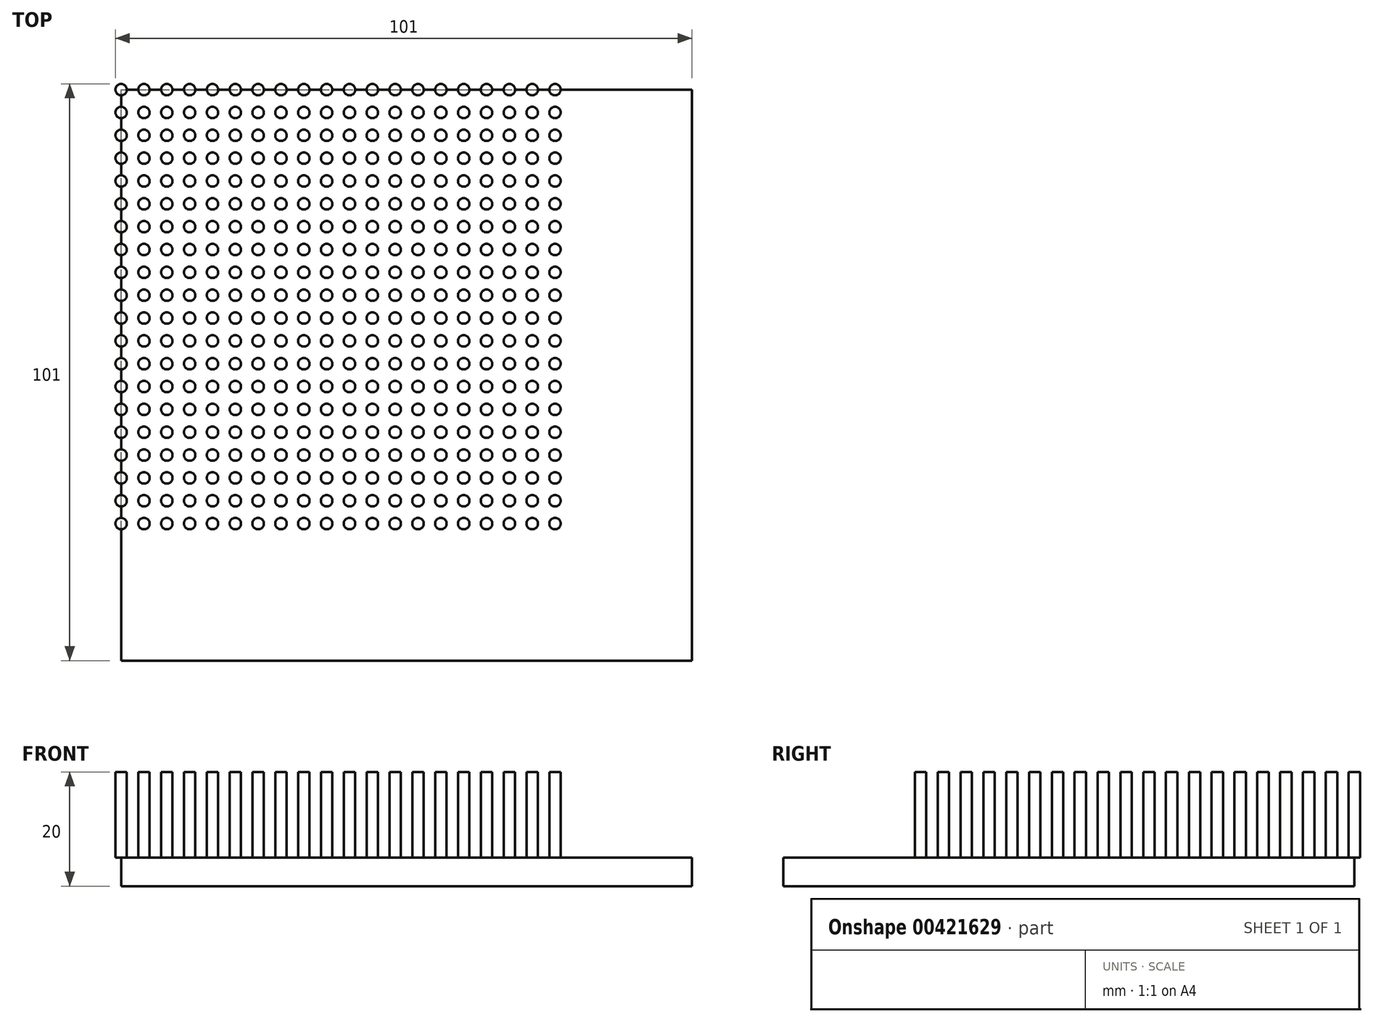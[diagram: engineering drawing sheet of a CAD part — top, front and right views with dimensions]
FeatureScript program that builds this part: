
annotation { "Feature Type Name" : "Feature", "Feature Type Description" : "" }
export const myFeature = defineFeature(function(context is Context, id is Id, definition is map)
    precondition{}
    {
        {
            var Q0;
            Q0=qCreatedBy(makeId("Top.planeOp"),FACE);
            var sketch = newSketch(context, id + "F0", { "sketchPlane" : qUnion([Q0])});
            skLineSegment(sketch, "E0.bottom", {"start": v(0, 0) * mm, "end": v(100, 0) * mm});
            skLineSegment(sketch, "E0.top", {"start": v(0, 100) * mm, "end": v(100, 100) * mm});
            skLineSegment(sketch, "E0.left", {"start": v(0, 0) * mm, "end": v(0, 100) * mm});
            skLineSegment(sketch, "E0.right", {"start": v(100, 0) * mm, "end": v(100, 100) * mm});
            skSolve(sketch);
        }
        {
            var Q0;
            Q0 = qSketchRegion(id + "F0", true);
            extrude(context, id + "F1", {"entities" : qUnion([Q0]), "depth" : 5 * mm});
        }
        {
            var Q0;
            Q0=makeQuery(id+"F1.opExtrude","CAP_FACE",FACE,{"disambiguationData":[OSD([sQuery(id+"F0.wireOp",EDGE,"E0.bottom"),sQuery(id+"F0.wireOp",EDGE,"E0.top"),sQuery(id+"F0.wireOp",EDGE,"E0.left"),sQuery(id+"F0.wireOp",EDGE,"E0.right")])],"isStart":false});
            var sketch = newSketch(context, id + "F2", { "sketchPlane" : qUnion([Q0])});
            skCircle(sketch, "E1", {"center": v(0, 100) * mm, "radius": 1 * mm});
            skCircle(sketch, "E2.0.1.0", {"center": v(0, 96) * mm, "radius": 1 * mm});
            skCircle(sketch, "E2.0.2.0", {"center": v(0, 92) * mm, "radius": 1 * mm});
            skCircle(sketch, "E2.0.3.0", {"center": v(0, 88) * mm, "radius": 1 * mm});
            skCircle(sketch, "E2.0.4.0", {"center": v(0, 84) * mm, "radius": 1 * mm});
            skCircle(sketch, "E2.0.5.0", {"center": v(0, 80) * mm, "radius": 1 * mm});
            skCircle(sketch, "E2.0.6.0", {"center": v(0, 76) * mm, "radius": 1 * mm});
            skCircle(sketch, "E2.0.7.0", {"center": v(0, 72) * mm, "radius": 1 * mm});
            skCircle(sketch, "E2.0.8.0", {"center": v(0, 68) * mm, "radius": 1 * mm});
            skCircle(sketch, "E2.0.9.0", {"center": v(0, 64) * mm, "radius": 1 * mm});
            skCircle(sketch, "E2.0.10.0", {"center": v(0, 60) * mm, "radius": 1 * mm});
            skCircle(sketch, "E2.0.11.0", {"center": v(0, 56) * mm, "radius": 1 * mm});
            skCircle(sketch, "E2.0.12.0", {"center": v(0, 52) * mm, "radius": 1 * mm});
            skCircle(sketch, "E2.0.13.0", {"center": v(0, 48) * mm, "radius": 1 * mm});
            skCircle(sketch, "E2.0.14.0", {"center": v(0, 44) * mm, "radius": 1 * mm});
            skCircle(sketch, "E2.0.15.0", {"center": v(0, 40) * mm, "radius": 1 * mm});
            skCircle(sketch, "E2.0.16.0", {"center": v(0, 36) * mm, "radius": 1 * mm});
            skCircle(sketch, "E2.0.17.0", {"center": v(0, 32) * mm, "radius": 1 * mm});
            skCircle(sketch, "E2.0.18.0", {"center": v(0, 28) * mm, "radius": 1 * mm});
            skCircle(sketch, "E2.0.19.0", {"center": v(0, 24) * mm, "radius": 1 * mm});
            skCircle(sketch, "E2.1.0.0", {"center": v(4, 100) * mm, "radius": 1 * mm});
            skCircle(sketch, "E2.1.1.0", {"center": v(4, 96) * mm, "radius": 1 * mm});
            skCircle(sketch, "E2.1.2.0", {"center": v(4, 92) * mm, "radius": 1 * mm});
            skCircle(sketch, "E2.1.3.0", {"center": v(4, 88) * mm, "radius": 1 * mm});
            skCircle(sketch, "E2.1.4.0", {"center": v(4, 84) * mm, "radius": 1 * mm});
            skCircle(sketch, "E2.1.5.0", {"center": v(4, 80) * mm, "radius": 1 * mm});
            skCircle(sketch, "E2.1.6.0", {"center": v(4, 76) * mm, "radius": 1 * mm});
            skCircle(sketch, "E2.1.7.0", {"center": v(4, 72) * mm, "radius": 1 * mm});
            skCircle(sketch, "E2.1.8.0", {"center": v(4, 68) * mm, "radius": 1 * mm});
            skCircle(sketch, "E2.1.9.0", {"center": v(4, 64) * mm, "radius": 1 * mm});
            skCircle(sketch, "E2.1.10.0", {"center": v(4, 60) * mm, "radius": 1 * mm});
            skCircle(sketch, "E2.1.11.0", {"center": v(4, 56) * mm, "radius": 1 * mm});
            skCircle(sketch, "E2.1.12.0", {"center": v(4, 52) * mm, "radius": 1 * mm});
            skCircle(sketch, "E2.1.13.0", {"center": v(4, 48) * mm, "radius": 1 * mm});
            skCircle(sketch, "E2.1.14.0", {"center": v(4, 44) * mm, "radius": 1 * mm});
            skCircle(sketch, "E2.1.15.0", {"center": v(4, 40) * mm, "radius": 1 * mm});
            skCircle(sketch, "E2.1.16.0", {"center": v(4, 36) * mm, "radius": 1 * mm});
            skCircle(sketch, "E2.1.17.0", {"center": v(4, 32) * mm, "radius": 1 * mm});
            skCircle(sketch, "E2.1.18.0", {"center": v(4, 28) * mm, "radius": 1 * mm});
            skCircle(sketch, "E2.1.19.0", {"center": v(4, 24) * mm, "radius": 1 * mm});
            skCircle(sketch, "E2.2.0.0", {"center": v(8, 100) * mm, "radius": 1 * mm});
            skCircle(sketch, "E2.2.1.0", {"center": v(8, 96) * mm, "radius": 1 * mm});
            skCircle(sketch, "E2.2.2.0", {"center": v(8, 92) * mm, "radius": 1 * mm});
            skCircle(sketch, "E2.2.3.0", {"center": v(8, 88) * mm, "radius": 1 * mm});
            skCircle(sketch, "E2.2.4.0", {"center": v(8, 84) * mm, "radius": 1 * mm});
            skCircle(sketch, "E2.2.5.0", {"center": v(8, 80) * mm, "radius": 1 * mm});
            skCircle(sketch, "E2.2.6.0", {"center": v(8, 76) * mm, "radius": 1 * mm});
            skCircle(sketch, "E2.2.7.0", {"center": v(8, 72) * mm, "radius": 1 * mm});
            skCircle(sketch, "E2.2.8.0", {"center": v(8, 68) * mm, "radius": 1 * mm});
            skCircle(sketch, "E2.2.9.0", {"center": v(8, 64) * mm, "radius": 1 * mm});
            skCircle(sketch, "E2.2.10.0", {"center": v(8, 60) * mm, "radius": 1 * mm});
            skCircle(sketch, "E2.2.11.0", {"center": v(8, 56) * mm, "radius": 1 * mm});
            skCircle(sketch, "E2.2.12.0", {"center": v(8, 52) * mm, "radius": 1 * mm});
            skCircle(sketch, "E2.2.13.0", {"center": v(8, 48) * mm, "radius": 1 * mm});
            skCircle(sketch, "E2.2.14.0", {"center": v(8, 44) * mm, "radius": 1 * mm});
            skCircle(sketch, "E2.2.15.0", {"center": v(8, 40) * mm, "radius": 1 * mm});
            skCircle(sketch, "E2.2.16.0", {"center": v(8, 36) * mm, "radius": 1 * mm});
            skCircle(sketch, "E2.2.17.0", {"center": v(8, 32) * mm, "radius": 1 * mm});
            skCircle(sketch, "E2.2.18.0", {"center": v(8, 28) * mm, "radius": 1 * mm});
            skCircle(sketch, "E2.2.19.0", {"center": v(8, 24) * mm, "radius": 1 * mm});
            skCircle(sketch, "E2.3.0.0", {"center": v(12, 100) * mm, "radius": 1 * mm});
            skCircle(sketch, "E2.3.1.0", {"center": v(12, 96) * mm, "radius": 1 * mm});
            skCircle(sketch, "E2.3.2.0", {"center": v(12, 92) * mm, "radius": 1 * mm});
            skCircle(sketch, "E2.3.3.0", {"center": v(12, 88) * mm, "radius": 1 * mm});
            skCircle(sketch, "E2.3.4.0", {"center": v(12, 84) * mm, "radius": 1 * mm});
            skCircle(sketch, "E2.3.5.0", {"center": v(12, 80) * mm, "radius": 1 * mm});
            skCircle(sketch, "E2.3.6.0", {"center": v(12, 76) * mm, "radius": 1 * mm});
            skCircle(sketch, "E2.3.7.0", {"center": v(12, 72) * mm, "radius": 1 * mm});
            skCircle(sketch, "E2.3.8.0", {"center": v(12, 68) * mm, "radius": 1 * mm});
            skCircle(sketch, "E2.3.9.0", {"center": v(12, 64) * mm, "radius": 1 * mm});
            skCircle(sketch, "E2.3.10.0", {"center": v(12, 60) * mm, "radius": 1 * mm});
            skCircle(sketch, "E2.3.11.0", {"center": v(12, 56) * mm, "radius": 1 * mm});
            skCircle(sketch, "E2.3.12.0", {"center": v(12, 52) * mm, "radius": 1 * mm});
            skCircle(sketch, "E2.3.13.0", {"center": v(12, 48) * mm, "radius": 1 * mm});
            skCircle(sketch, "E2.3.14.0", {"center": v(12, 44) * mm, "radius": 1 * mm});
            skCircle(sketch, "E2.3.15.0", {"center": v(12, 40) * mm, "radius": 1 * mm});
            skCircle(sketch, "E2.3.16.0", {"center": v(12, 36) * mm, "radius": 1 * mm});
            skCircle(sketch, "E2.3.17.0", {"center": v(12, 32) * mm, "radius": 1 * mm});
            skCircle(sketch, "E2.3.18.0", {"center": v(12, 28) * mm, "radius": 1 * mm});
            skCircle(sketch, "E2.3.19.0", {"center": v(12, 24) * mm, "radius": 1 * mm});
            skCircle(sketch, "E2.4.0.0", {"center": v(16, 100) * mm, "radius": 1 * mm});
            skCircle(sketch, "E2.4.1.0", {"center": v(16, 96) * mm, "radius": 1 * mm});
            skCircle(sketch, "E2.4.2.0", {"center": v(16, 92) * mm, "radius": 1 * mm});
            skCircle(sketch, "E2.4.3.0", {"center": v(16, 88) * mm, "radius": 1 * mm});
            skCircle(sketch, "E2.4.4.0", {"center": v(16, 84) * mm, "radius": 1 * mm});
            skCircle(sketch, "E2.4.5.0", {"center": v(16, 80) * mm, "radius": 1 * mm});
            skCircle(sketch, "E2.4.6.0", {"center": v(16, 76) * mm, "radius": 1 * mm});
            skCircle(sketch, "E2.4.7.0", {"center": v(16, 72) * mm, "radius": 1 * mm});
            skCircle(sketch, "E2.4.8.0", {"center": v(16, 68) * mm, "radius": 1 * mm});
            skCircle(sketch, "E2.4.9.0", {"center": v(16, 64) * mm, "radius": 1 * mm});
            skCircle(sketch, "E2.4.10.0", {"center": v(16, 60) * mm, "radius": 1 * mm});
            skCircle(sketch, "E2.4.11.0", {"center": v(16, 56) * mm, "radius": 1 * mm});
            skCircle(sketch, "E2.4.12.0", {"center": v(16, 52) * mm, "radius": 1 * mm});
            skCircle(sketch, "E2.4.13.0", {"center": v(16, 48) * mm, "radius": 1 * mm});
            skCircle(sketch, "E2.4.14.0", {"center": v(16, 44) * mm, "radius": 1 * mm});
            skCircle(sketch, "E2.4.15.0", {"center": v(16, 40) * mm, "radius": 1 * mm});
            skCircle(sketch, "E2.4.16.0", {"center": v(16, 36) * mm, "radius": 1 * mm});
            skCircle(sketch, "E2.4.17.0", {"center": v(16, 32) * mm, "radius": 1 * mm});
            skCircle(sketch, "E2.4.18.0", {"center": v(16, 28) * mm, "radius": 1 * mm});
            skCircle(sketch, "E2.4.19.0", {"center": v(16, 24) * mm, "radius": 1 * mm});
            skCircle(sketch, "E2.5.0.0", {"center": v(20, 100) * mm, "radius": 1 * mm});
            skCircle(sketch, "E2.5.1.0", {"center": v(20, 96) * mm, "radius": 1 * mm});
            skCircle(sketch, "E2.5.2.0", {"center": v(20, 92) * mm, "radius": 1 * mm});
            skCircle(sketch, "E2.5.3.0", {"center": v(20, 88) * mm, "radius": 1 * mm});
            skCircle(sketch, "E2.5.4.0", {"center": v(20, 84) * mm, "radius": 1 * mm});
            skCircle(sketch, "E2.5.5.0", {"center": v(20, 80) * mm, "radius": 1 * mm});
            skCircle(sketch, "E2.5.6.0", {"center": v(20, 76) * mm, "radius": 1 * mm});
            skCircle(sketch, "E2.5.7.0", {"center": v(20, 72) * mm, "radius": 1 * mm});
            skCircle(sketch, "E2.5.8.0", {"center": v(20, 68) * mm, "radius": 1 * mm});
            skCircle(sketch, "E2.5.9.0", {"center": v(20, 64) * mm, "radius": 1 * mm});
            skCircle(sketch, "E2.5.10.0", {"center": v(20, 60) * mm, "radius": 1 * mm});
            skCircle(sketch, "E2.5.11.0", {"center": v(20, 56) * mm, "radius": 1 * mm});
            skCircle(sketch, "E2.5.12.0", {"center": v(20, 52) * mm, "radius": 1 * mm});
            skCircle(sketch, "E2.5.13.0", {"center": v(20, 48) * mm, "radius": 1 * mm});
            skCircle(sketch, "E2.5.14.0", {"center": v(20, 44) * mm, "radius": 1 * mm});
            skCircle(sketch, "E2.5.15.0", {"center": v(20, 40) * mm, "radius": 1 * mm});
            skCircle(sketch, "E2.5.16.0", {"center": v(20, 36) * mm, "radius": 1 * mm});
            skCircle(sketch, "E2.5.17.0", {"center": v(20, 32) * mm, "radius": 1 * mm});
            skCircle(sketch, "E2.5.18.0", {"center": v(20, 28) * mm, "radius": 1 * mm});
            skCircle(sketch, "E2.5.19.0", {"center": v(20, 24) * mm, "radius": 1 * mm});
            skCircle(sketch, "E2.6.0.0", {"center": v(24, 100) * mm, "radius": 1 * mm});
            skCircle(sketch, "E2.6.1.0", {"center": v(24, 96) * mm, "radius": 1 * mm});
            skCircle(sketch, "E2.6.2.0", {"center": v(24, 92) * mm, "radius": 1 * mm});
            skCircle(sketch, "E2.6.3.0", {"center": v(24, 88) * mm, "radius": 1 * mm});
            skCircle(sketch, "E2.6.4.0", {"center": v(24, 84) * mm, "radius": 1 * mm});
            skCircle(sketch, "E2.6.5.0", {"center": v(24, 80) * mm, "radius": 1 * mm});
            skCircle(sketch, "E2.6.6.0", {"center": v(24, 76) * mm, "radius": 1 * mm});
            skCircle(sketch, "E2.6.7.0", {"center": v(24, 72) * mm, "radius": 1 * mm});
            skCircle(sketch, "E2.6.8.0", {"center": v(24, 68) * mm, "radius": 1 * mm});
            skCircle(sketch, "E2.6.9.0", {"center": v(24, 64) * mm, "radius": 1 * mm});
            skCircle(sketch, "E2.6.10.0", {"center": v(24, 60) * mm, "radius": 1 * mm});
            skCircle(sketch, "E2.6.11.0", {"center": v(24, 56) * mm, "radius": 1 * mm});
            skCircle(sketch, "E2.6.12.0", {"center": v(24, 52) * mm, "radius": 1 * mm});
            skCircle(sketch, "E2.6.13.0", {"center": v(24, 48) * mm, "radius": 1 * mm});
            skCircle(sketch, "E2.6.14.0", {"center": v(24, 44) * mm, "radius": 1 * mm});
            skCircle(sketch, "E2.6.15.0", {"center": v(24, 40) * mm, "radius": 1 * mm});
            skCircle(sketch, "E2.6.16.0", {"center": v(24, 36) * mm, "radius": 1 * mm});
            skCircle(sketch, "E2.6.17.0", {"center": v(24, 32) * mm, "radius": 1 * mm});
            skCircle(sketch, "E2.6.18.0", {"center": v(24, 28) * mm, "radius": 1 * mm});
            skCircle(sketch, "E2.6.19.0", {"center": v(24, 24) * mm, "radius": 1 * mm});
            skCircle(sketch, "E2.7.0.0", {"center": v(28, 100) * mm, "radius": 1 * mm});
            skCircle(sketch, "E2.7.1.0", {"center": v(28, 96) * mm, "radius": 1 * mm});
            skCircle(sketch, "E2.7.2.0", {"center": v(28, 92) * mm, "radius": 1 * mm});
            skCircle(sketch, "E2.7.3.0", {"center": v(28, 88) * mm, "radius": 1 * mm});
            skCircle(sketch, "E2.7.4.0", {"center": v(28, 84) * mm, "radius": 1 * mm});
            skCircle(sketch, "E2.7.5.0", {"center": v(28, 80) * mm, "radius": 1 * mm});
            skCircle(sketch, "E2.7.6.0", {"center": v(28, 76) * mm, "radius": 1 * mm});
            skCircle(sketch, "E2.7.7.0", {"center": v(28, 72) * mm, "radius": 1 * mm});
            skCircle(sketch, "E2.7.8.0", {"center": v(28, 68) * mm, "radius": 1 * mm});
            skCircle(sketch, "E2.7.9.0", {"center": v(28, 64) * mm, "radius": 1 * mm});
            skCircle(sketch, "E2.7.10.0", {"center": v(28, 60) * mm, "radius": 1 * mm});
            skCircle(sketch, "E2.7.11.0", {"center": v(28, 56) * mm, "radius": 1 * mm});
            skCircle(sketch, "E2.7.12.0", {"center": v(28, 52) * mm, "radius": 1 * mm});
            skCircle(sketch, "E2.7.13.0", {"center": v(28, 48) * mm, "radius": 1 * mm});
            skCircle(sketch, "E2.7.14.0", {"center": v(28, 44) * mm, "radius": 1 * mm});
            skCircle(sketch, "E2.7.15.0", {"center": v(28, 40) * mm, "radius": 1 * mm});
            skCircle(sketch, "E2.7.16.0", {"center": v(28, 36) * mm, "radius": 1 * mm});
            skCircle(sketch, "E2.7.17.0", {"center": v(28, 32) * mm, "radius": 1 * mm});
            skCircle(sketch, "E2.7.18.0", {"center": v(28, 28) * mm, "radius": 1 * mm});
            skCircle(sketch, "E2.7.19.0", {"center": v(28, 24) * mm, "radius": 1 * mm});
            skCircle(sketch, "E2.8.0.0", {"center": v(32, 100) * mm, "radius": 1 * mm});
            skCircle(sketch, "E2.8.1.0", {"center": v(32, 96) * mm, "radius": 1 * mm});
            skCircle(sketch, "E2.8.2.0", {"center": v(32, 92) * mm, "radius": 1 * mm});
            skCircle(sketch, "E2.8.3.0", {"center": v(32, 88) * mm, "radius": 1 * mm});
            skCircle(sketch, "E2.8.4.0", {"center": v(32, 84) * mm, "radius": 1 * mm});
            skCircle(sketch, "E2.8.5.0", {"center": v(32, 80) * mm, "radius": 1 * mm});
            skCircle(sketch, "E2.8.6.0", {"center": v(32, 76) * mm, "radius": 1 * mm});
            skCircle(sketch, "E2.8.7.0", {"center": v(32, 72) * mm, "radius": 1 * mm});
            skCircle(sketch, "E2.8.8.0", {"center": v(32, 68) * mm, "radius": 1 * mm});
            skCircle(sketch, "E2.8.9.0", {"center": v(32, 64) * mm, "radius": 1 * mm});
            skCircle(sketch, "E2.8.10.0", {"center": v(32, 60) * mm, "radius": 1 * mm});
            skCircle(sketch, "E2.8.11.0", {"center": v(32, 56) * mm, "radius": 1 * mm});
            skCircle(sketch, "E2.8.12.0", {"center": v(32, 52) * mm, "radius": 1 * mm});
            skCircle(sketch, "E2.8.13.0", {"center": v(32, 48) * mm, "radius": 1 * mm});
            skCircle(sketch, "E2.8.14.0", {"center": v(32, 44) * mm, "radius": 1 * mm});
            skCircle(sketch, "E2.8.15.0", {"center": v(32, 40) * mm, "radius": 1 * mm});
            skCircle(sketch, "E2.8.16.0", {"center": v(32, 36) * mm, "radius": 1 * mm});
            skCircle(sketch, "E2.8.17.0", {"center": v(32, 32) * mm, "radius": 1 * mm});
            skCircle(sketch, "E2.8.18.0", {"center": v(32, 28) * mm, "radius": 1 * mm});
            skCircle(sketch, "E2.8.19.0", {"center": v(32, 24) * mm, "radius": 1 * mm});
            skCircle(sketch, "E2.9.0.0", {"center": v(36, 100) * mm, "radius": 1 * mm});
            skCircle(sketch, "E2.9.1.0", {"center": v(36, 96) * mm, "radius": 1 * mm});
            skCircle(sketch, "E2.9.2.0", {"center": v(36, 92) * mm, "radius": 1 * mm});
            skCircle(sketch, "E2.9.3.0", {"center": v(36, 88) * mm, "radius": 1 * mm});
            skCircle(sketch, "E2.9.4.0", {"center": v(36, 84) * mm, "radius": 1 * mm});
            skCircle(sketch, "E2.9.5.0", {"center": v(36, 80) * mm, "radius": 1 * mm});
            skCircle(sketch, "E2.9.6.0", {"center": v(36, 76) * mm, "radius": 1 * mm});
            skCircle(sketch, "E2.9.7.0", {"center": v(36, 72) * mm, "radius": 1 * mm});
            skCircle(sketch, "E2.9.8.0", {"center": v(36, 68) * mm, "radius": 1 * mm});
            skCircle(sketch, "E2.9.9.0", {"center": v(36, 64) * mm, "radius": 1 * mm});
            skCircle(sketch, "E2.9.10.0", {"center": v(36, 60) * mm, "radius": 1 * mm});
            skCircle(sketch, "E2.9.11.0", {"center": v(36, 56) * mm, "radius": 1 * mm});
            skCircle(sketch, "E2.9.12.0", {"center": v(36, 52) * mm, "radius": 1 * mm});
            skCircle(sketch, "E2.9.13.0", {"center": v(36, 48) * mm, "radius": 1 * mm});
            skCircle(sketch, "E2.9.14.0", {"center": v(36, 44) * mm, "radius": 1 * mm});
            skCircle(sketch, "E2.9.15.0", {"center": v(36, 40) * mm, "radius": 1 * mm});
            skCircle(sketch, "E2.9.16.0", {"center": v(36, 36) * mm, "radius": 1 * mm});
            skCircle(sketch, "E2.9.17.0", {"center": v(36, 32) * mm, "radius": 1 * mm});
            skCircle(sketch, "E2.9.18.0", {"center": v(36, 28) * mm, "radius": 1 * mm});
            skCircle(sketch, "E2.9.19.0", {"center": v(36, 24) * mm, "radius": 1 * mm});
            skCircle(sketch, "E2.10.0.0", {"center": v(40, 100) * mm, "radius": 1 * mm});
            skCircle(sketch, "E2.10.1.0", {"center": v(40, 96) * mm, "radius": 1 * mm});
            skCircle(sketch, "E2.10.2.0", {"center": v(40, 92) * mm, "radius": 1 * mm});
            skCircle(sketch, "E2.10.3.0", {"center": v(40, 88) * mm, "radius": 1 * mm});
            skCircle(sketch, "E2.10.4.0", {"center": v(40, 84) * mm, "radius": 1 * mm});
            skCircle(sketch, "E2.10.5.0", {"center": v(40, 80) * mm, "radius": 1 * mm});
            skCircle(sketch, "E2.10.6.0", {"center": v(40, 76) * mm, "radius": 1 * mm});
            skCircle(sketch, "E2.10.7.0", {"center": v(40, 72) * mm, "radius": 1 * mm});
            skCircle(sketch, "E2.10.8.0", {"center": v(40, 68) * mm, "radius": 1 * mm});
            skCircle(sketch, "E2.10.9.0", {"center": v(40, 64) * mm, "radius": 1 * mm});
            skCircle(sketch, "E2.10.10.0", {"center": v(40, 60) * mm, "radius": 1 * mm});
            skCircle(sketch, "E2.10.11.0", {"center": v(40, 56) * mm, "radius": 1 * mm});
            skCircle(sketch, "E2.10.12.0", {"center": v(40, 52) * mm, "radius": 1 * mm});
            skCircle(sketch, "E2.10.13.0", {"center": v(40, 48) * mm, "radius": 1 * mm});
            skCircle(sketch, "E2.10.14.0", {"center": v(40, 44) * mm, "radius": 1 * mm});
            skCircle(sketch, "E2.10.15.0", {"center": v(40, 40) * mm, "radius": 1 * mm});
            skCircle(sketch, "E2.10.16.0", {"center": v(40, 36) * mm, "radius": 1 * mm});
            skCircle(sketch, "E2.10.17.0", {"center": v(40, 32) * mm, "radius": 1 * mm});
            skCircle(sketch, "E2.10.18.0", {"center": v(40, 28) * mm, "radius": 1 * mm});
            skCircle(sketch, "E2.10.19.0", {"center": v(40, 24) * mm, "radius": 1 * mm});
            skCircle(sketch, "E2.11.0.0", {"center": v(44, 100) * mm, "radius": 1 * mm});
            skCircle(sketch, "E2.11.1.0", {"center": v(44, 96) * mm, "radius": 1 * mm});
            skCircle(sketch, "E2.11.2.0", {"center": v(44, 92) * mm, "radius": 1 * mm});
            skCircle(sketch, "E2.11.3.0", {"center": v(44, 88) * mm, "radius": 1 * mm});
            skCircle(sketch, "E2.11.4.0", {"center": v(44, 84) * mm, "radius": 1 * mm});
            skCircle(sketch, "E2.11.5.0", {"center": v(44, 80) * mm, "radius": 1 * mm});
            skCircle(sketch, "E2.11.6.0", {"center": v(44, 76) * mm, "radius": 1 * mm});
            skCircle(sketch, "E2.11.7.0", {"center": v(44, 72) * mm, "radius": 1 * mm});
            skCircle(sketch, "E2.11.8.0", {"center": v(44, 68) * mm, "radius": 1 * mm});
            skCircle(sketch, "E2.11.9.0", {"center": v(44, 64) * mm, "radius": 1 * mm});
            skCircle(sketch, "E2.11.10.0", {"center": v(44, 60) * mm, "radius": 1 * mm});
            skCircle(sketch, "E2.11.11.0", {"center": v(44, 56) * mm, "radius": 1 * mm});
            skCircle(sketch, "E2.11.12.0", {"center": v(44, 52) * mm, "radius": 1 * mm});
            skCircle(sketch, "E2.11.13.0", {"center": v(44, 48) * mm, "radius": 1 * mm});
            skCircle(sketch, "E2.11.14.0", {"center": v(44, 44) * mm, "radius": 1 * mm});
            skCircle(sketch, "E2.11.15.0", {"center": v(44, 40) * mm, "radius": 1 * mm});
            skCircle(sketch, "E2.11.16.0", {"center": v(44, 36) * mm, "radius": 1 * mm});
            skCircle(sketch, "E2.11.17.0", {"center": v(44, 32) * mm, "radius": 1 * mm});
            skCircle(sketch, "E2.11.18.0", {"center": v(44, 28) * mm, "radius": 1 * mm});
            skCircle(sketch, "E2.11.19.0", {"center": v(44, 24) * mm, "radius": 1 * mm});
            skCircle(sketch, "E2.12.0.0", {"center": v(48, 100) * mm, "radius": 1 * mm});
            skCircle(sketch, "E2.12.1.0", {"center": v(48, 96) * mm, "radius": 1 * mm});
            skCircle(sketch, "E2.12.2.0", {"center": v(48, 92) * mm, "radius": 1 * mm});
            skCircle(sketch, "E2.12.3.0", {"center": v(48, 88) * mm, "radius": 1 * mm});
            skCircle(sketch, "E2.12.4.0", {"center": v(48, 84) * mm, "radius": 1 * mm});
            skCircle(sketch, "E2.12.5.0", {"center": v(48, 80) * mm, "radius": 1 * mm});
            skCircle(sketch, "E2.12.6.0", {"center": v(48, 76) * mm, "radius": 1 * mm});
            skCircle(sketch, "E2.12.7.0", {"center": v(48, 72) * mm, "radius": 1 * mm});
            skCircle(sketch, "E2.12.8.0", {"center": v(48, 68) * mm, "radius": 1 * mm});
            skCircle(sketch, "E2.12.9.0", {"center": v(48, 64) * mm, "radius": 1 * mm});
            skCircle(sketch, "E2.12.10.0", {"center": v(48, 60) * mm, "radius": 1 * mm});
            skCircle(sketch, "E2.12.11.0", {"center": v(48, 56) * mm, "radius": 1 * mm});
            skCircle(sketch, "E2.12.12.0", {"center": v(48, 52) * mm, "radius": 1 * mm});
            skCircle(sketch, "E2.12.13.0", {"center": v(48, 48) * mm, "radius": 1 * mm});
            skCircle(sketch, "E2.12.14.0", {"center": v(48, 44) * mm, "radius": 1 * mm});
            skCircle(sketch, "E2.12.15.0", {"center": v(48, 40) * mm, "radius": 1 * mm});
            skCircle(sketch, "E2.12.16.0", {"center": v(48, 36) * mm, "radius": 1 * mm});
            skCircle(sketch, "E2.12.17.0", {"center": v(48, 32) * mm, "radius": 1 * mm});
            skCircle(sketch, "E2.12.18.0", {"center": v(48, 28) * mm, "radius": 1 * mm});
            skCircle(sketch, "E2.12.19.0", {"center": v(48, 24) * mm, "radius": 1 * mm});
            skCircle(sketch, "E2.13.0.0", {"center": v(52, 100) * mm, "radius": 1 * mm});
            skCircle(sketch, "E2.13.1.0", {"center": v(52, 96) * mm, "radius": 1 * mm});
            skCircle(sketch, "E2.13.2.0", {"center": v(52, 92) * mm, "radius": 1 * mm});
            skCircle(sketch, "E2.13.3.0", {"center": v(52, 88) * mm, "radius": 1 * mm});
            skCircle(sketch, "E2.13.4.0", {"center": v(52, 84) * mm, "radius": 1 * mm});
            skCircle(sketch, "E2.13.5.0", {"center": v(52, 80) * mm, "radius": 1 * mm});
            skCircle(sketch, "E2.13.6.0", {"center": v(52, 76) * mm, "radius": 1 * mm});
            skCircle(sketch, "E2.13.7.0", {"center": v(52, 72) * mm, "radius": 1 * mm});
            skCircle(sketch, "E2.13.8.0", {"center": v(52, 68) * mm, "radius": 1 * mm});
            skCircle(sketch, "E2.13.9.0", {"center": v(52, 64) * mm, "radius": 1 * mm});
            skCircle(sketch, "E2.13.10.0", {"center": v(52, 60) * mm, "radius": 1 * mm});
            skCircle(sketch, "E2.13.11.0", {"center": v(52, 56) * mm, "radius": 1 * mm});
            skCircle(sketch, "E2.13.12.0", {"center": v(52, 52) * mm, "radius": 1 * mm});
            skCircle(sketch, "E2.13.13.0", {"center": v(52, 48) * mm, "radius": 1 * mm});
            skCircle(sketch, "E2.13.14.0", {"center": v(52, 44) * mm, "radius": 1 * mm});
            skCircle(sketch, "E2.13.15.0", {"center": v(52, 40) * mm, "radius": 1 * mm});
            skCircle(sketch, "E2.13.16.0", {"center": v(52, 36) * mm, "radius": 1 * mm});
            skCircle(sketch, "E2.13.17.0", {"center": v(52, 32) * mm, "radius": 1 * mm});
            skCircle(sketch, "E2.13.18.0", {"center": v(52, 28) * mm, "radius": 1 * mm});
            skCircle(sketch, "E2.13.19.0", {"center": v(52, 24) * mm, "radius": 1 * mm});
            skCircle(sketch, "E2.14.0.0", {"center": v(56, 100) * mm, "radius": 1 * mm});
            skCircle(sketch, "E2.14.1.0", {"center": v(56, 96) * mm, "radius": 1 * mm});
            skCircle(sketch, "E2.14.2.0", {"center": v(56, 92) * mm, "radius": 1 * mm});
            skCircle(sketch, "E2.14.3.0", {"center": v(56, 88) * mm, "radius": 1 * mm});
            skCircle(sketch, "E2.14.4.0", {"center": v(56, 84) * mm, "radius": 1 * mm});
            skCircle(sketch, "E2.14.5.0", {"center": v(56, 80) * mm, "radius": 1 * mm});
            skCircle(sketch, "E2.14.6.0", {"center": v(56, 76) * mm, "radius": 1 * mm});
            skCircle(sketch, "E2.14.7.0", {"center": v(56, 72) * mm, "radius": 1 * mm});
            skCircle(sketch, "E2.14.8.0", {"center": v(56, 68) * mm, "radius": 1 * mm});
            skCircle(sketch, "E2.14.9.0", {"center": v(56, 64) * mm, "radius": 1 * mm});
            skCircle(sketch, "E2.14.10.0", {"center": v(56, 60) * mm, "radius": 1 * mm});
            skCircle(sketch, "E2.14.11.0", {"center": v(56, 56) * mm, "radius": 1 * mm});
            skCircle(sketch, "E2.14.12.0", {"center": v(56, 52) * mm, "radius": 1 * mm});
            skCircle(sketch, "E2.14.13.0", {"center": v(56, 48) * mm, "radius": 1 * mm});
            skCircle(sketch, "E2.14.14.0", {"center": v(56, 44) * mm, "radius": 1 * mm});
            skCircle(sketch, "E2.14.15.0", {"center": v(56, 40) * mm, "radius": 1 * mm});
            skCircle(sketch, "E2.14.16.0", {"center": v(56, 36) * mm, "radius": 1 * mm});
            skCircle(sketch, "E2.14.17.0", {"center": v(56, 32) * mm, "radius": 1 * mm});
            skCircle(sketch, "E2.14.18.0", {"center": v(56, 28) * mm, "radius": 1 * mm});
            skCircle(sketch, "E2.14.19.0", {"center": v(56, 24) * mm, "radius": 1 * mm});
            skCircle(sketch, "E2.15.0.0", {"center": v(60, 100) * mm, "radius": 1 * mm});
            skCircle(sketch, "E2.15.1.0", {"center": v(60, 96) * mm, "radius": 1 * mm});
            skCircle(sketch, "E2.15.2.0", {"center": v(60, 92) * mm, "radius": 1 * mm});
            skCircle(sketch, "E2.15.3.0", {"center": v(60, 88) * mm, "radius": 1 * mm});
            skCircle(sketch, "E2.15.4.0", {"center": v(60, 84) * mm, "radius": 1 * mm});
            skCircle(sketch, "E2.15.5.0", {"center": v(60, 80) * mm, "radius": 1 * mm});
            skCircle(sketch, "E2.15.6.0", {"center": v(60, 76) * mm, "radius": 1 * mm});
            skCircle(sketch, "E2.15.7.0", {"center": v(60, 72) * mm, "radius": 1 * mm});
            skCircle(sketch, "E2.15.8.0", {"center": v(60, 68) * mm, "radius": 1 * mm});
            skCircle(sketch, "E2.15.9.0", {"center": v(60, 64) * mm, "radius": 1 * mm});
            skCircle(sketch, "E2.15.10.0", {"center": v(60, 60) * mm, "radius": 1 * mm});
            skCircle(sketch, "E2.15.11.0", {"center": v(60, 56) * mm, "radius": 1 * mm});
            skCircle(sketch, "E2.15.12.0", {"center": v(60, 52) * mm, "radius": 1 * mm});
            skCircle(sketch, "E2.15.13.0", {"center": v(60, 48) * mm, "radius": 1 * mm});
            skCircle(sketch, "E2.15.14.0", {"center": v(60, 44) * mm, "radius": 1 * mm});
            skCircle(sketch, "E2.15.15.0", {"center": v(60, 40) * mm, "radius": 1 * mm});
            skCircle(sketch, "E2.15.16.0", {"center": v(60, 36) * mm, "radius": 1 * mm});
            skCircle(sketch, "E2.15.17.0", {"center": v(60, 32) * mm, "radius": 1 * mm});
            skCircle(sketch, "E2.15.18.0", {"center": v(60, 28) * mm, "radius": 1 * mm});
            skCircle(sketch, "E2.15.19.0", {"center": v(60, 24) * mm, "radius": 1 * mm});
            skCircle(sketch, "E2.16.0.0", {"center": v(64, 100) * mm, "radius": 1 * mm});
            skCircle(sketch, "E2.16.1.0", {"center": v(64, 96) * mm, "radius": 1 * mm});
            skCircle(sketch, "E2.16.2.0", {"center": v(64, 92) * mm, "radius": 1 * mm});
            skCircle(sketch, "E2.16.3.0", {"center": v(64, 88) * mm, "radius": 1 * mm});
            skCircle(sketch, "E2.16.4.0", {"center": v(64, 84) * mm, "radius": 1 * mm});
            skCircle(sketch, "E2.16.5.0", {"center": v(64, 80) * mm, "radius": 1 * mm});
            skCircle(sketch, "E2.16.6.0", {"center": v(64, 76) * mm, "radius": 1 * mm});
            skCircle(sketch, "E2.16.7.0", {"center": v(64, 72) * mm, "radius": 1 * mm});
            skCircle(sketch, "E2.16.8.0", {"center": v(64, 68) * mm, "radius": 1 * mm});
            skCircle(sketch, "E2.16.9.0", {"center": v(64, 64) * mm, "radius": 1 * mm});
            skCircle(sketch, "E2.16.10.0", {"center": v(64, 60) * mm, "radius": 1 * mm});
            skCircle(sketch, "E2.16.11.0", {"center": v(64, 56) * mm, "radius": 1 * mm});
            skCircle(sketch, "E2.16.12.0", {"center": v(64, 52) * mm, "radius": 1 * mm});
            skCircle(sketch, "E2.16.13.0", {"center": v(64, 48) * mm, "radius": 1 * mm});
            skCircle(sketch, "E2.16.14.0", {"center": v(64, 44) * mm, "radius": 1 * mm});
            skCircle(sketch, "E2.16.15.0", {"center": v(64, 40) * mm, "radius": 1 * mm});
            skCircle(sketch, "E2.16.16.0", {"center": v(64, 36) * mm, "radius": 1 * mm});
            skCircle(sketch, "E2.16.17.0", {"center": v(64, 32) * mm, "radius": 1 * mm});
            skCircle(sketch, "E2.16.18.0", {"center": v(64, 28) * mm, "radius": 1 * mm});
            skCircle(sketch, "E2.16.19.0", {"center": v(64, 24) * mm, "radius": 1 * mm});
            skCircle(sketch, "E2.17.0.0", {"center": v(68, 100) * mm, "radius": 1 * mm});
            skCircle(sketch, "E2.17.1.0", {"center": v(68, 96) * mm, "radius": 1 * mm});
            skCircle(sketch, "E2.17.2.0", {"center": v(68, 92) * mm, "radius": 1 * mm});
            skCircle(sketch, "E2.17.3.0", {"center": v(68, 88) * mm, "radius": 1 * mm});
            skCircle(sketch, "E2.17.4.0", {"center": v(68, 84) * mm, "radius": 1 * mm});
            skCircle(sketch, "E2.17.5.0", {"center": v(68, 80) * mm, "radius": 1 * mm});
            skCircle(sketch, "E2.17.6.0", {"center": v(68, 76) * mm, "radius": 1 * mm});
            skCircle(sketch, "E2.17.7.0", {"center": v(68, 72) * mm, "radius": 1 * mm});
            skCircle(sketch, "E2.17.8.0", {"center": v(68, 68) * mm, "radius": 1 * mm});
            skCircle(sketch, "E2.17.9.0", {"center": v(68, 64) * mm, "radius": 1 * mm});
            skCircle(sketch, "E2.17.10.0", {"center": v(68, 60) * mm, "radius": 1 * mm});
            skCircle(sketch, "E2.17.11.0", {"center": v(68, 56) * mm, "radius": 1 * mm});
            skCircle(sketch, "E2.17.12.0", {"center": v(68, 52) * mm, "radius": 1 * mm});
            skCircle(sketch, "E2.17.13.0", {"center": v(68, 48) * mm, "radius": 1 * mm});
            skCircle(sketch, "E2.17.14.0", {"center": v(68, 44) * mm, "radius": 1 * mm});
            skCircle(sketch, "E2.17.15.0", {"center": v(68, 40) * mm, "radius": 1 * mm});
            skCircle(sketch, "E2.17.16.0", {"center": v(68, 36) * mm, "radius": 1 * mm});
            skCircle(sketch, "E2.17.17.0", {"center": v(68, 32) * mm, "radius": 1 * mm});
            skCircle(sketch, "E2.17.18.0", {"center": v(68, 28) * mm, "radius": 1 * mm});
            skCircle(sketch, "E2.17.19.0", {"center": v(68, 24) * mm, "radius": 1 * mm});
            skCircle(sketch, "E2.18.0.0", {"center": v(72, 100) * mm, "radius": 1 * mm});
            skCircle(sketch, "E2.18.1.0", {"center": v(72, 96) * mm, "radius": 1 * mm});
            skCircle(sketch, "E2.18.2.0", {"center": v(72, 92) * mm, "radius": 1 * mm});
            skCircle(sketch, "E2.18.3.0", {"center": v(72, 88) * mm, "radius": 1 * mm});
            skCircle(sketch, "E2.18.4.0", {"center": v(72, 84) * mm, "radius": 1 * mm});
            skCircle(sketch, "E2.18.5.0", {"center": v(72, 80) * mm, "radius": 1 * mm});
            skCircle(sketch, "E2.18.6.0", {"center": v(72, 76) * mm, "radius": 1 * mm});
            skCircle(sketch, "E2.18.7.0", {"center": v(72, 72) * mm, "radius": 1 * mm});
            skCircle(sketch, "E2.18.8.0", {"center": v(72, 68) * mm, "radius": 1 * mm});
            skCircle(sketch, "E2.18.9.0", {"center": v(72, 64) * mm, "radius": 1 * mm});
            skCircle(sketch, "E2.18.10.0", {"center": v(72, 60) * mm, "radius": 1 * mm});
            skCircle(sketch, "E2.18.11.0", {"center": v(72, 56) * mm, "radius": 1 * mm});
            skCircle(sketch, "E2.18.12.0", {"center": v(72, 52) * mm, "radius": 1 * mm});
            skCircle(sketch, "E2.18.13.0", {"center": v(72, 48) * mm, "radius": 1 * mm});
            skCircle(sketch, "E2.18.14.0", {"center": v(72, 44) * mm, "radius": 1 * mm});
            skCircle(sketch, "E2.18.15.0", {"center": v(72, 40) * mm, "radius": 1 * mm});
            skCircle(sketch, "E2.18.16.0", {"center": v(72, 36) * mm, "radius": 1 * mm});
            skCircle(sketch, "E2.18.17.0", {"center": v(72, 32) * mm, "radius": 1 * mm});
            skCircle(sketch, "E2.18.18.0", {"center": v(72, 28) * mm, "radius": 1 * mm});
            skCircle(sketch, "E2.18.19.0", {"center": v(72, 24) * mm, "radius": 1 * mm});
            skCircle(sketch, "E2.19.0.0", {"center": v(76, 100) * mm, "radius": 1 * mm});
            skCircle(sketch, "E2.19.1.0", {"center": v(76, 96) * mm, "radius": 1 * mm});
            skCircle(sketch, "E2.19.2.0", {"center": v(76, 92) * mm, "radius": 1 * mm});
            skCircle(sketch, "E2.19.3.0", {"center": v(76, 88) * mm, "radius": 1 * mm});
            skCircle(sketch, "E2.19.4.0", {"center": v(76, 84) * mm, "radius": 1 * mm});
            skCircle(sketch, "E2.19.5.0", {"center": v(76, 80) * mm, "radius": 1 * mm});
            skCircle(sketch, "E2.19.6.0", {"center": v(76, 76) * mm, "radius": 1 * mm});
            skCircle(sketch, "E2.19.7.0", {"center": v(76, 72) * mm, "radius": 1 * mm});
            skCircle(sketch, "E2.19.8.0", {"center": v(76, 68) * mm, "radius": 1 * mm});
            skCircle(sketch, "E2.19.9.0", {"center": v(76, 64) * mm, "radius": 1 * mm});
            skCircle(sketch, "E2.19.10.0", {"center": v(76, 60) * mm, "radius": 1 * mm});
            skCircle(sketch, "E2.19.11.0", {"center": v(76, 56) * mm, "radius": 1 * mm});
            skCircle(sketch, "E2.19.12.0", {"center": v(76, 52) * mm, "radius": 1 * mm});
            skCircle(sketch, "E2.19.13.0", {"center": v(76, 48) * mm, "radius": 1 * mm});
            skCircle(sketch, "E2.19.14.0", {"center": v(76, 44) * mm, "radius": 1 * mm});
            skCircle(sketch, "E2.19.15.0", {"center": v(76, 40) * mm, "radius": 1 * mm});
            skCircle(sketch, "E2.19.16.0", {"center": v(76, 36) * mm, "radius": 1 * mm});
            skCircle(sketch, "E2.19.17.0", {"center": v(76, 32) * mm, "radius": 1 * mm});
            skCircle(sketch, "E2.19.18.0", {"center": v(76, 28) * mm, "radius": 1 * mm});
            skCircle(sketch, "E2.19.19.0", {"center": v(76, 24) * mm, "radius": 1 * mm});
            skLineSegment(sketch, "E2.direction1", {"start": v(0, 100) * mm, "end": v(4, 100) * mm, "construction": true});
            skLineSegment(sketch, "E2.direction2", {"start": v(0, 100) * mm, "end": v(0, 96) * mm, "construction": true});
            skSolve(sketch);
        }
        {
            var Q0;
            Q0 = qSketchRegion(id + "F2", true);
            extrude(context, id + "F3", {"entities" : qUnion([Q0]), "operationType" : NewBodyOperationType.ADD, "depth" : 15 * mm});
        }
    });
